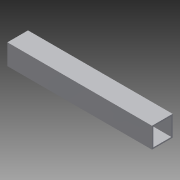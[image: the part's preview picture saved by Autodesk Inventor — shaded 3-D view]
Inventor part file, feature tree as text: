
AUTODESK INVENTOR PART (.ipt)
format: ipt  version: 2014 (Build 180170000, 170)  size: 86,528 bytes
history: native  units: in
note: dims shown in document units (in); Inventor stores cm internally (conversion verified against a paired STEP export)
features: extrude x1, sketch x1
ambient origin geometry x8: Origin, YZ Plane, XZ Plane, XY Plane, X Axis, Y Axis, Z Axis, Center Point
bodies: Solid1 (feature_tree)
feature tree (2):
  extrude  "Extrusion1"  Depth=1.0in
  sketch  "Sketch1"  dims[d0=1.0in d1=1.0in d2=0.0625in d3=7.0in d4=0.0in]
